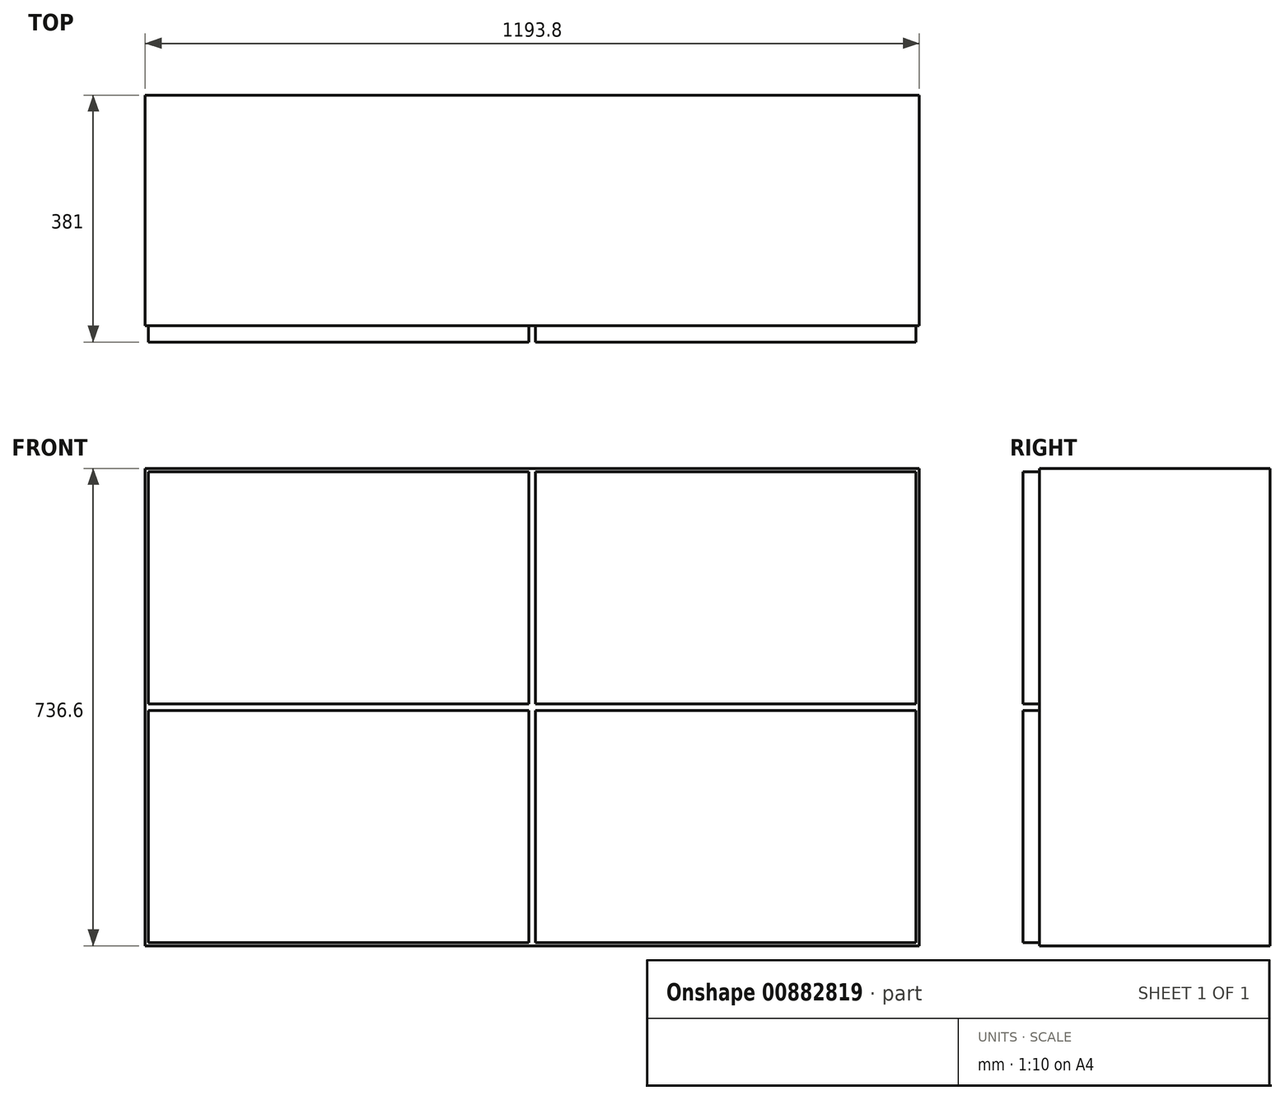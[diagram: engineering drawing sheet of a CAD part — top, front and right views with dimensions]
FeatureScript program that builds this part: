
annotation { "Feature Type Name" : "Feature", "Feature Type Description" : "" }
export const myFeature = defineFeature(function(context is Context, id is Id, definition is map)
    precondition{}
    {
        {
            var Q0;
            Q0=qCreatedBy(makeId("Front.planeOp"),FACE);
            var sketch = newSketch(context, id + "F0", { "sketchPlane" : qUnion([Q0])});
            skLineSegment(sketch, "E0.bottom", {"start": v(-596.9, 368.3) * mm, "end": v(596.9, 368.3) * mm});
            skLineSegment(sketch, "E0.top", {"start": v(-596.9, -368.3) * mm, "end": v(596.9, -368.3) * mm});
            skLineSegment(sketch, "E0.left", {"start": v(-596.9, 368.3) * mm, "end": v(-596.9, -368.3) * mm});
            skLineSegment(sketch, "E0.right", {"start": v(596.9, 368.3) * mm, "end": v(596.9, -368.3) * mm});
            skPoint(sketch, "E0.middle", {"position": v(0, 0) * mm});
            skSolve(sketch);
        }
        {
            var Q0;
            Q0 = qSketchRegion(id + "F0", true);
            extrude(context, id + "F1", {"entities" : qUnion([Q0]), "depth" : 355.6 * mm, "offsetDistance" : 25.4 * mm});
        }
        {
            var Q0;
            Q0=makeQuery(id+"F1.opExtrude","CAP_FACE",FACE,{"disambiguationData":[OSD([sQuery(id+"F0.wireOp",EDGE,"E0.bottom"),sQuery(id+"F0.wireOp",EDGE,"E0.top"),sQuery(id+"F0.wireOp",EDGE,"E0.left"),sQuery(id+"F0.wireOp",EDGE,"E0.right")])],"isStart":false});
            var sketch = newSketch(context, id + "F2", { "sketchPlane" : qUnion([Q0])});
            skLineSegment(sketch, "E1.bottom", {"start": v(-596.9, 368.3) * mm, "end": v(-591.82, 368.3) * mm});
            skLineSegment(sketch, "E1.top", {"start": v(-596.9, 363.22) * mm, "end": v(-591.82, 363.22) * mm});
            skLineSegment(sketch, "E1.left", {"start": v(-596.9, 368.3) * mm, "end": v(-596.9, 363.22) * mm});
            skLineSegment(sketch, "E1.right", {"start": v(-591.82, 368.3) * mm, "end": v(-591.82, 363.22) * mm});
            skLineSegment(sketch, "E2.bottom", {"start": v(5.08, -5.08) * mm, "end": v(-5.08, -5.08) * mm});
            skLineSegment(sketch, "E2.top", {"start": v(5.08, 5.08) * mm, "end": v(-5.08, 5.08) * mm});
            skLineSegment(sketch, "E2.left", {"start": v(5.08, -5.08) * mm, "end": v(5.08, 5.08) * mm});
            skLineSegment(sketch, "E2.right", {"start": v(-5.08, -5.08) * mm, "end": v(-5.08, 5.08) * mm});
            skPoint(sketch, "E2.middle", {"position": v(0, 0) * mm});
            skLineSegment(sketch, "E3.bottom", {"start": v(-591.82, 363.22) * mm, "end": v(-5.08, 363.22) * mm});
            skLineSegment(sketch, "E3.top", {"start": v(-591.82, 5.08) * mm, "end": v(-5.08, 5.08) * mm});
            skLineSegment(sketch, "E3.left", {"start": v(-591.82, 363.22) * mm, "end": v(-591.82, 5.08) * mm});
            skLineSegment(sketch, "E3.right", {"start": v(-5.08, 363.22) * mm, "end": v(-5.08, 5.08) * mm});
            skLineSegment(sketch, "E4.0.1.0", {"start": v(-5.08, -5.08) * mm, "end": v(-5.08, -363.22) * mm});
            skLineSegment(sketch, "E4.0.1.1", {"start": v(-591.82, -363.22) * mm, "end": v(-5.08, -363.22) * mm});
            skLineSegment(sketch, "E4.0.1.2", {"start": v(-591.82, -5.08) * mm, "end": v(-591.82, -363.22) * mm});
            skLineSegment(sketch, "E4.0.1.3", {"start": v(-591.82, -5.08) * mm, "end": v(-5.08, -5.08) * mm});
            skLineSegment(sketch, "E4.1.0.0", {"start": v(591.82, 363.22) * mm, "end": v(591.82, 5.08) * mm});
            skLineSegment(sketch, "E4.1.0.1", {"start": v(5.08, 5.08) * mm, "end": v(591.82, 5.08) * mm});
            skLineSegment(sketch, "E4.1.0.2", {"start": v(5.08, 363.22) * mm, "end": v(5.08, 5.08) * mm});
            skLineSegment(sketch, "E4.1.0.3", {"start": v(5.08, 363.22) * mm, "end": v(591.82, 363.22) * mm});
            skLineSegment(sketch, "E4.1.1.0", {"start": v(591.82, -5.08) * mm, "end": v(591.82, -363.22) * mm});
            skLineSegment(sketch, "E4.1.1.1", {"start": v(5.08, -363.22) * mm, "end": v(591.82, -363.22) * mm});
            skLineSegment(sketch, "E4.1.1.2", {"start": v(5.08, -5.08) * mm, "end": v(5.08, -363.22) * mm});
            skLineSegment(sketch, "E4.1.1.3", {"start": v(5.08, -5.08) * mm, "end": v(591.82, -5.08) * mm});
            skLineSegment(sketch, "E4.direction1", {"start": v(-5.08, 5.08) * mm, "end": v(591.82, 5.08) * mm, "construction": true});
            skLineSegment(sketch, "E4.direction2", {"start": v(-5.08, 5.08) * mm, "end": v(-5.08, -363.22) * mm, "construction": true});
            skSolve(sketch);
        }
        {
            var Q0;
            Q0=makeQuery(id+"F2.imprint","IMPRINT",FACE,{"disambiguationData":[TD([[makeQuery(id+"F2.imprint","IMPRINT",EDGE,{"derivedFrom":sQuery(id+"F2.wireOp",EDGE,"E4.1.0.0")}),-1.0]])]});
            var Q1;
            Q1=makeQuery(id+"F2.imprint","IMPRINT",FACE,{"disambiguationData":[TD([[makeQuery(id+"F2.imprint","IMPRINT",EDGE,{"derivedFrom":sQuery(id+"F2.wireOp",EDGE,"E4.1.1.0")}),-1.0]])]});
            var Q2;
            Q2=makeQuery(id+"F2.imprint","IMPRINT",FACE,{"disambiguationData":[TD([[makeQuery(id+"F2.imprint","IMPRINT",EDGE,{"derivedFrom":sQuery(id+"F2.wireOp",EDGE,"E4.0.1.0")}),-1.0]])]});
            var Q3;
            Q3=makeQuery(id+"F2.imprint","IMPRINT",FACE,{"disambiguationData":[TD([[makeQuery(id+"F2.imprint","IMPRINT",EDGE,{"derivedFrom":sQuery(id+"F2.wireOp",EDGE,"E3.bottom")}),-1.0]])]});
            extrude(context, id + "F3", {"entities" : qUnion([Q0, Q1, Q2, Q3]), "operationType" : NewBodyOperationType.ADD, "depth" : 25.4 * mm, "offsetDistance" : 25.4 * mm});
        }
    });
